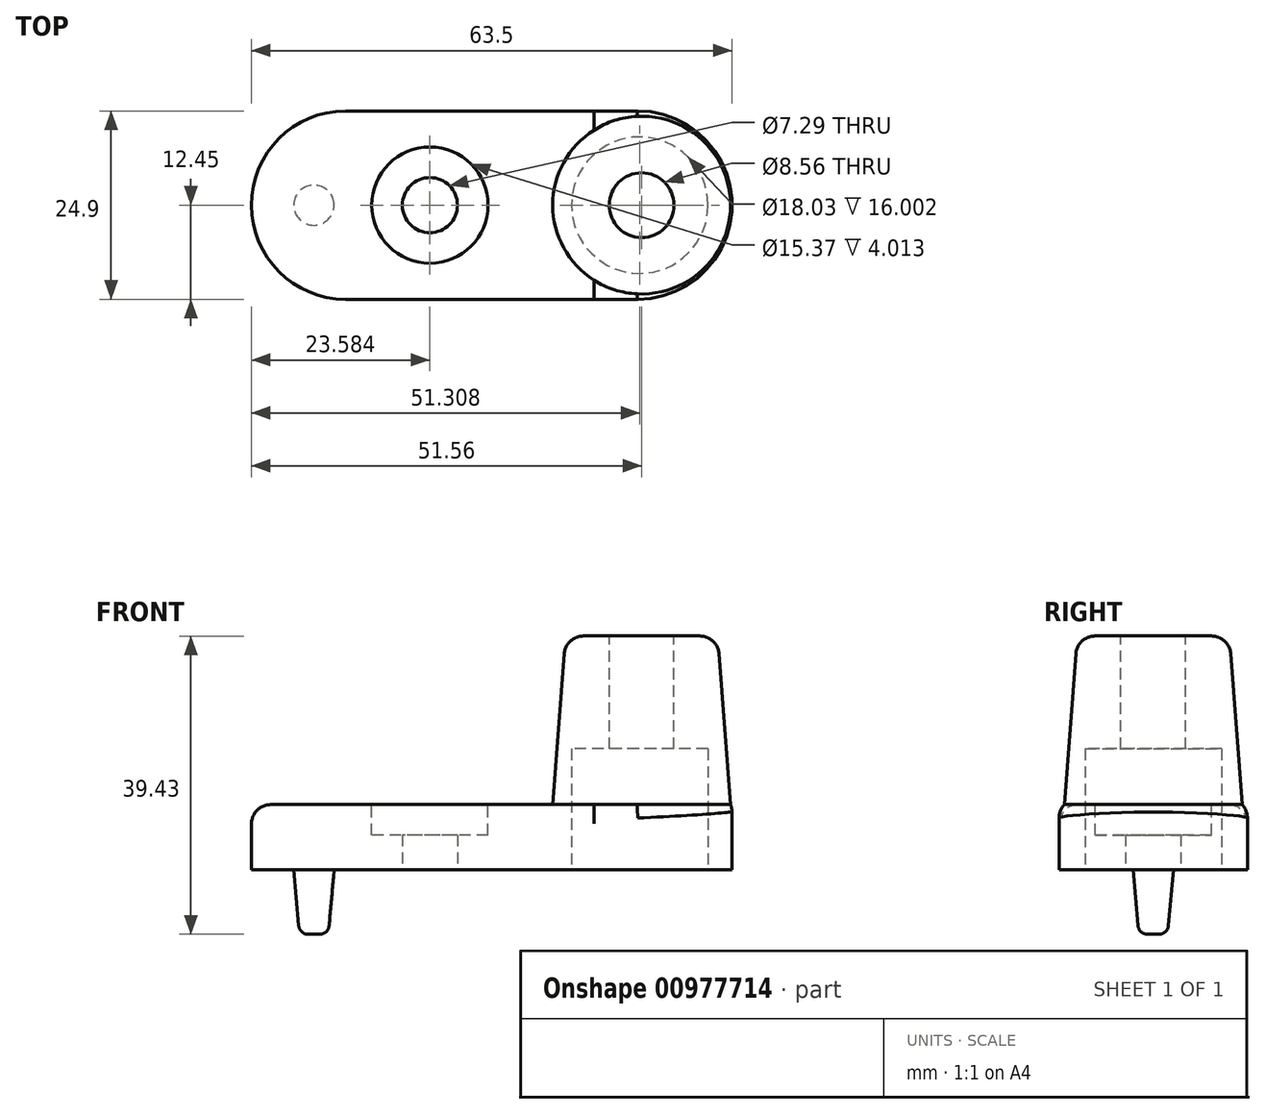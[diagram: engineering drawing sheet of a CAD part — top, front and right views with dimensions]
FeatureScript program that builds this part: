
annotation { "Feature Type Name" : "Feature", "Feature Type Description" : "" }
export const myFeature = defineFeature(function(context is Context, id is Id, definition is map)
    precondition{}
    {
        {
            var Q0;
            Q0=qCreatedBy(makeId("Top.planeOp"),FACE);
            var sketch = newSketch(context, id + "F0", { "sketchPlane" : qUnion([Q0])});
            skLineSegment(sketch, "E0.bottom", {"start": v(19.3, 12.45) * mm, "end": v(-19.3, 12.45) * mm});
            skLineSegment(sketch, "E0.top", {"start": v(19.3, -12.45) * mm, "end": v(-19.3, -12.45) * mm});
            skLineSegment(sketch, "E0.left", {"start": v(31.75, 0) * mm, "end": v(31.75, 0) * mm});
            skLineSegment(sketch, "E0.right", {"start": v(-31.75, 0) * mm, "end": v(-31.75, 0) * mm});
            skPoint(sketch, "E0.middle", {"position": v(0, 0) * mm});
            skPoint(sketch, "E1.visualSharp", {"position": v(-31.75, 12.45) * mm});
            skArc(sketch, "E1.filletArc", {"start": v(-19.3, 12.45) * mm, "mid": v(-28.1, 8.8) * mm, "end": v(-31.75, 0) * mm});
            skPoint(sketch, "E2.visualSharp", {"position": v(31.75, 12.45) * mm});
            skArc(sketch, "E2.filletArc", {"start": v(31.75, 0) * mm, "mid": v(28.1, 8.8) * mm, "end": v(19.3, 12.45) * mm});
            skPoint(sketch, "E3.visualSharp", {"position": v(-31.75, -12.45) * mm});
            skArc(sketch, "E3.filletArc", {"start": v(-31.75, 0) * mm, "mid": v(-28.1, -8.8) * mm, "end": v(-19.3, -12.45) * mm});
            skPoint(sketch, "E4.visualSharp", {"position": v(31.75, -12.45) * mm});
            skArc(sketch, "E4.filletArc", {"start": v(19.3, -12.45) * mm, "mid": v(28.1, -8.8) * mm, "end": v(31.75, 0) * mm});
            skCircle(sketch, "E5", {"center": v(-23.5, 0) * mm, "radius": 2.67 * mm});
            skCircle(sketch, "E6", {"center": v(19.56, 0) * mm, "radius": 9.02 * mm});
            skCircle(sketch, "E7", {"center": v(19.56, 0) * mm, "radius": 4.06 * mm});
            skCircle(sketch, "E8", {"center": v(-8.17, 0) * mm, "radius": 3.64 * mm});
            skSolve(sketch);
        }
        {
            var Q0;
            Q0=makeQuery(id+"F0.imprint","IMPRINT",FACE,{"disambiguationData":[TD([[makeQuery(id+"F0.imprint","IMPRINT",EDGE,{"derivedFrom":sQuery(id+"F0.wireOp",EDGE,"E0.bottom")}),1.0]])]});
            var Q1;
            Q1=makeQuery(id+"F0.imprint","IMPRINT",FACE,{"disambiguationData":[TD([[makeQuery(id+"F0.imprint","IMPRINT",EDGE,{"derivedFrom":sQuery(id+"F0.wireOp",EDGE,"E6")}),1.0]])]});
            var Q2;
            Q2=makeQuery(id+"F0.imprint","IMPRINT",FACE,{"disambiguationData":[TD([[makeQuery(id+"F0.imprint","IMPRINT",EDGE,{"derivedFrom":sQuery(id+"F0.wireOp",EDGE,"E7")}),1.0]])]});
            var Q3;
            Q3=makeQuery(id+"F0.imprint","IMPRINT",FACE,{"disambiguationData":[TD([[makeQuery(id+"F0.imprint","IMPRINT",EDGE,{"derivedFrom":sQuery(id+"F0.wireOp",EDGE,"E5")}),1.0]])]});
            extrude(context, id + "F1", {"entities" : qUnion([Q0, Q1, Q2, Q3]), "depth" : 8.64 * mm, "offsetDistance" : 25.4 * mm});
        }
        {
            var Q0;
            Q0=makeQuery(id+"F1.opExtrude","CAP_FACE",FACE,{"disambiguationData":[OSD([sQuery(id+"F0.wireOp",EDGE,"E0.bottom"),sQuery(id+"F0.wireOp",EDGE,"E0.top"),sQuery(id+"F0.wireOp",EDGE,"E1.filletArc"),sQuery(id+"F0.wireOp",EDGE,"E2.filletArc"),sQuery(id+"F0.wireOp",EDGE,"E3.filletArc"),sQuery(id+"F0.wireOp",EDGE,"E4.filletArc"),sQuery(id+"F0.wireOp",EDGE,"E8"),sQuery(id+"F0.wireOp",EDGE,"E7")])],"isStart":false});
            var sketch = newSketch(context, id + "F2", { "sketchPlane" : qUnion([Q0])});
            skCircle(sketch, "E9.0", {"center": v(19.56, 0) * mm, "radius": 4.06 * mm});
            skCircle(sketch, "E10", {"center": v(19.56, 0) * mm, "radius": 11.62 * mm});
            skSolve(sketch);
        }
        {
            var Q0;
            Q0=qCreatedBy(makeId("Top.planeOp"),FACE);
            cPlane(context, id + "F3", {"entities" : qUnion([Q0]), "cplaneType" : CPlaneType.OFFSET, "offset" : 30.99 * mm, "width" : 152.4 * mm, "height" : 152.4 * mm});
        }
        {
            var Q0;
            Q0=qCreatedBy(makeId("Front.planeOp"),FACE);
            var sketch = newSketch(context, id + "F4", { "sketchPlane" : qUnion([Q0])});
            skLineSegment(sketch, "E11", {"start": v(8.06, 8.58) * mm, "end": v(9.76, 30.92) * mm});
            skLineSegment(sketch, "E12", {"start": v(9.76, 30.92) * mm, "end": v(15.53, 30.92) * mm});
            skLineSegment(sketch, "E13", {"start": v(15.53, 30.92) * mm, "end": v(15.53, 8.54) * mm});
            skLineSegment(sketch, "E14", {"start": v(15.53, 8.54) * mm, "end": v(8.06, 8.58) * mm});
            skLineSegment(sketch, "E15", {"start": v(19.81, 31.02) * mm, "end": v(19.81, 8.62) * mm});
            skSolve(sketch);
        }
        {
            var Q0;
            Q0=makeQuery(id+"F4.imprint","IMPRINT",FACE,{"disambiguationData":[TD([[makeQuery(id+"F4.imprint","IMPRINT",EDGE,{"derivedFrom":sQuery(id+"F4.wireOp",EDGE,"E11")}),-1.0]])]});
            var Q1;
            Q1=sQuery(id+"F4.wireOp",EDGE,"E15");
            revolve(context, id + "F5", {"operationType" : NewBodyOperationType.ADD, "surfaceOperationType" : NewSurfaceOperationType.NEW, "entities" : qUnion([Q0]), "axis" : qUnion([Q1]), "revolveType" : RevolveType.FULL});
        }
        {
            var Q0;
            Q0=makeQuery(id+"F1.opExtrude","CAP_EDGE",EDGE,{"disambiguationData":[OSD([sQuery(id+"F0.wireOp",EDGE,"E0.top")])],"isStart":false});
            var Q1;
            Q1=makeQuery(id+"F5.opRevolve","SWEPT_EDGE",EDGE,{"disambiguationData":[OSD([sQuery(id+"F4.wireOp",EDGE,"E11"),sQuery(id+"F4.wireOp",EDGE,"E12")])]});
            fillet(context, id + "F6", {"entities" : qUnion([Q0, Q1]), "radius" : 2.54 * mm, "tangentPropagation" : true, "allowEdgeOverflow" : false});
        }
        {
            var Q0;
            Q0=makeQuery(id+"F0.imprint","IMPRINT",FACE,{"disambiguationData":[TD([[makeQuery(id+"F0.imprint","IMPRINT",EDGE,{"derivedFrom":sQuery(id+"F0.wireOp",EDGE,"E6")}),1.0]])]});
            var Q1;
            Q1=makeQuery(id+"F0.imprint","IMPRINT",FACE,{"disambiguationData":[TD([[makeQuery(id+"F0.imprint","IMPRINT",EDGE,{"derivedFrom":sQuery(id+"F0.wireOp",EDGE,"E7")}),1.0]])]});
            extrude(context, id + "F7", {"entities" : qUnion([Q0, Q1]), "operationType" : NewBodyOperationType.REMOVE, "depth" : 16 * mm, "offsetDistance" : 25.4 * mm});
        }
        {
            var Q0;
            Q0=makeQuery(id+"F2.imprint","IMPRINT",FACE,{"disambiguationData":[TD([[makeQuery(id+"F2.imprint","IMPRINT",EDGE,{"derivedFrom":sQuery(id+"F2.wireOp",EDGE,"E10")}),-1.0]])]});
            var sketch = newSketch(context, id + "F8", { "sketchPlane" : qUnion([Q0])});
            skCircle(sketch, "E16.0", {"center": v(-8.17, 0) * mm, "radius": 3.64 * mm});
            skCircle(sketch, "E17", {"center": v(-8.17, 0) * mm, "radius": 7.68 * mm});
            skSolve(sketch);
        }
        {
            var Q0;
            Q0=makeQuery(id+"F8.imprint","IMPRINT",FACE,{"disambiguationData":[TD([[makeQuery(id+"F8.imprint","IMPRINT",EDGE,{"derivedFrom":sQuery(id+"F8.wireOp",EDGE,"E16.0")}),-1.0]])]});
            extrude(context, id + "F9", {"entities" : qUnion([Q0]), "operationType" : NewBodyOperationType.REMOVE, "oppositeDirection" : true, "depth" : 4 * mm, "offsetDistance" : 25.4 * mm});
        }
        {
            var Q0;
            Q0=qCreatedBy(makeId("Front.planeOp"),FACE);
            var sketch = newSketch(context, id + "F10", { "sketchPlane" : qUnion([Q0])});
            skLineSegment(sketch, "E18.0", {"start": v(-26.16, 0) * mm, "end": v(-20.83, 0) * mm});
            skLineSegment(sketch, "E19", {"start": v(-23.5, 0) * mm, "end": v(-23.5, -8.5) * mm});
            skLineSegment(sketch, "E20", {"start": v(-23.5, -8.5) * mm, "end": v(-25.4, -8.5) * mm});
            skLineSegment(sketch, "E21", {"start": v(-25.4, -8.5) * mm, "end": v(-26.16, 0) * mm});
            skSolve(sketch);
        }
        {
            var Q0;
            Q0 = qSketchRegion(id + "F10", true);
            var Q1;
            Q1=sQuery(id+"F10.wireOp",EDGE,"E19");
            revolve(context, id + "F11", {"operationType" : NewBodyOperationType.ADD, "surfaceOperationType" : NewSurfaceOperationType.NEW, "entities" : qUnion([Q0]), "axis" : qUnion([Q1]), "revolveType" : RevolveType.FULL});
        }
        {
            var Q0;
            Q0=makeQuery(id+"F11.opRevolve","SWEPT_EDGE",EDGE,{"disambiguationData":[OSD([sQuery(id+"F10.wireOp",EDGE,"E20"),sQuery(id+"F10.wireOp",EDGE,"E21")])]});
            fillet(context, id + "F12", {"entities" : qUnion([Q0]), "radius" : 1.27 * mm, "tangentPropagation" : true, "allowEdgeOverflow" : false});
        }
    });
